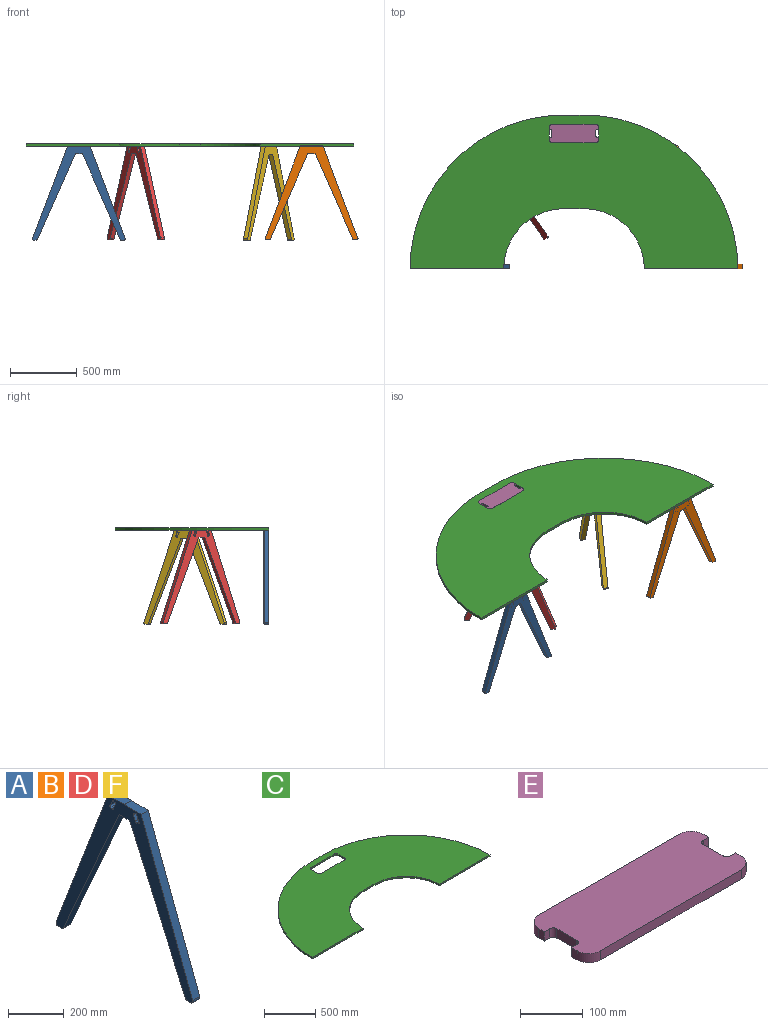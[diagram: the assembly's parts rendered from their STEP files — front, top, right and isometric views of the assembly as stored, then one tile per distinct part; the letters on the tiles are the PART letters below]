
ASSEMBLY  parts=6 mates=1
PART A: 38 faces, bbox 36x694.1x702 mm
  f0: plane 702.04x694.13mm, normal (-1,0,0), area 86384.5mm2, adj f1,f2,f3,f4,f5,f6,f7,f8
  f1: plane 36x27mm, normal (0,0,-1), area 971.9mm2, adj f0,f2,f18,f19
  f2: plane 36x0mm, normal (0,-0.85,0.53), area 0.2mm2, adj f0,f1,f3,f19
  f3: plane 638.9x282.02mm, normal (0,-0.91,-0.4), area 25141.4mm2, adj f0,f2,f4,f19
  f4: cylinder r=10mm len=36mm, axis (-1,0,0), area 415.8mm2, adj f0,f3,f5,f19
  f5: plane 36x18.89mm, normal (0,0,-1), area 680.2mm2, adj f0,f4,f6,f19
  f6: cylinder r=10mm len=36mm, axis (-1,0,0), area 696.3mm2, adj f0,f5,f7,f19
  f7: plane 688.47x261.77mm, normal (0,0.93,0.36), area 26516.1mm2, adj f0,f6,f8,f19
  f8: plane 82.88x36mm, normal (0,0,1), area 2983.7mm2, adj f0,f7,f9,f19
  f9: plane 36x0mm, normal (0,0.6,-0.8), area 0mm2, adj f0,f8,f10,f19
  f10: plane 36x1.76mm, normal (0,0,1), area 63.3mm2, adj f0,f9,f11,f19
  f11: plane 84.64x36mm, normal (0,0,1), area 3046.9mm2, adj f0,f10,f12,f19
  f12: plane 688.47x261.78mm, normal (0,-0.93,0.36), area 26516.1mm2, adj f0,f11,f13,f19
  f13: cylinder r=10mm len=36mm, axis (-1,0,0), area 696.3mm2, adj f0,f12,f14,f19
  f14: plane 36x18.89mm, normal (0,0,-1), area 680.2mm2, adj f0,f13,f15,f19
  f15: cylinder r=10mm len=36mm, axis (-1,0,0), area 415.8mm2, adj f0,f14,f16,f19
  f16: plane 636.51x280.97mm, normal (0,0.91,-0.4), area 25047.5mm2, adj f0,f15,f17,f19
  f17: cylinder r=4mm len=36mm, axis (-1,0,0), area 166.3mm2, adj f0,f16,f18,f19
  f18: plane 36x24.39mm, normal (0,0,-1), area 878mm2, adj f0,f1,f17,f19
  f19: plane 702.04x694.13mm, normal (1,0,0), area 87734.9mm2, adj f1,f2,f3,f4,f5,f6,f7,f8
  f20: cylinder r=4mm len=30mm, axis (-1,0,0), area 378.8mm2, adj f0,f21,f27,f28
  f21: plane 30x6.16mm, normal (0,0.39,-0.92), area 200.5mm2, adj f0,f20,f22,f28
  f22: cylinder r=4mm len=30mm, axis (-1,0,0), area 378.6mm2, adj f0,f21,f23,f28
  f23: plane 30x22.61mm, normal (0,0.92,0.39), area 738.2mm2, adj f0,f22,f24,f28
  f24: cylinder r=4mm len=30mm, axis (-1,0,0), area 378.6mm2, adj f0,f23,f25,f28
  f25: plane 30x5.8mm, normal (0,-0.39,0.92), area 188.5mm2, adj f0,f24,f26,f28
  f26: cylinder r=4mm len=30mm, axis (-1,0,0), area 378.8mm2, adj f0,f25,f27,f28
  f27: plane 30x22.77mm, normal (0,-0.93,-0.38), area 738.1mm2, adj f0,f20,f26,f28
  f28: plane 40.67x30.93mm, normal (-1,0,0), area 675.2mm2, adj f20,f21,f22,f23,f24,f25,f26,f27
  f29: plane 30x6.16mm, normal (0,-0.39,-0.92), area 200.5mm2, adj f0,f30,f36,f37
  f30: cylinder r=4mm len=30mm, axis (-1,0,0), area 378.8mm2, adj f0,f29,f31,f37
  f31: plane 30x22.77mm, normal (0,0.93,-0.38), area 738.1mm2, adj f0,f30,f32,f37
  f32: cylinder r=4mm len=30mm, axis (-1,0,0), area 378.8mm2, adj f0,f31,f33,f37
  f33: plane 30x5.8mm, normal (0,0.39,0.92), area 188.5mm2, adj f0,f32,f34,f37
  f34: cylinder r=4mm len=30mm, axis (-1,0,0), area 378.6mm2, adj f0,f33,f35,f37
  f35: plane 30x22.61mm, normal (0,-0.92,0.39), area 738.2mm2, adj f0,f34,f36,f37
  f36: cylinder r=4mm len=30mm, axis (-1,0,0), area 378.6mm2, adj f0,f29,f35,f37
  f37: plane 40.67x30.93mm, normal (-1,0,0), area 675.2mm2, adj f29,f30,f31,f32,f33,f34,f35,f36
PART B: same geometry as A
PART C: 18 faces, bbox 2450x1150x18 mm
  f0: cylinder r=26.8mm len=26.8mm, axis (0,0,-1), area 757.8mm2, adj f1,f15,f16,f17
  f1: plane 316x18mm, normal (0,1,0), area 5688mm2, adj f0,f2,f16,f17
  f2: cylinder r=26.8mm len=26.8mm, axis (0,0,-1), area 757.8mm2, adj f1,f3,f16,f17
  f3: plane 86x18mm, normal (1,0,0), area 1548mm2, adj f2,f4,f16,f17
  f4: cylinder r=26.8mm len=26.8mm, axis (0,0,-1), area 757.8mm2, adj f3,f5,f16,f17
  f5: plane 316x18mm, normal (0,-1,0), area 5688mm2, adj f4,f6,f16,f17
  f6: cylinder r=26.8mm len=26.8mm, axis (0,0,-1), area 757.8mm2, adj f5,f15,f16,f17
  f7: cylinder r=450mm len=450mm, axis (0,0,-1), area 12723.5mm2, adj f8,f14,f16,f17
  f8: plane 150x18mm, normal (0,-1,0), area 2700mm2, adj f7,f9,f16,f17
  f9: cylinder r=450mm len=450mm, axis (0,0,-1), area 12723.5mm2, adj f8,f10,f16,f17
  f10: plane 700x18mm, normal (0,-1,0), area 12600mm2, adj f9,f11,f16,f17
  f11: cylinder r=1150mm len=1150mm, axis (0,0,-1), area 32515.5mm2, adj f10,f12,f16,f17
  f12: plane 150x18mm, normal (0,1,0), area 2700mm2, adj f11,f13,f16,f17
  f13: cylinder r=1150mm len=1150mm, axis (0,0,-1), area 32515.5mm2, adj f12,f14,f16,f17
  f14: plane 700x18mm, normal (0,-1,0), area 12600mm2, adj f7,f13,f16,f17
  f15: plane 86x18mm, normal (-1,0,0), area 1548mm2, adj f0,f6,f16,f17
  f16: plane 2450x1150mm, normal (0,0,1), area 1813312.3mm2, adj f0,f1,f2,f3,f4,f5,f6,f7
  f17: plane 2450x1150mm, normal (0,0,-1), area 1813312.3mm2, adj f0,f1,f2,f3,f4,f5,f6,f7
PART D: same geometry as A
PART E: 22 faces, bbox 369x139.1x18 mm
  f0: cylinder r=8mm len=18mm, axis (0,0,-1), area 226.2mm2, adj f1,f19,f20,f21
  f1: plane 45x18mm, normal (1,0,0), area 810mm2, adj f0,f2,f20,f21
  f2: cylinder r=8mm len=18mm, axis (0,0,-1), area 226.2mm2, adj f1,f3,f20,f21
  f3: plane 18x12.11mm, normal (0,-1,0), area 218mm2, adj f2,f4,f20,f21
  f4: plane 18x12.5mm, normal (1,0,0), area 225mm2, adj f3,f5,f20,f21
  f5: cylinder r=26.5mm len=26.51mm, axis (0,0,-1), area 749.3mm2, adj f4,f6,f20,f21
  f6: plane 316x18mm, normal (0,1,0), area 5688mm2, adj f5,f7,f20,f21
  f7: cylinder r=26.5mm len=26.51mm, axis (0,0,-1), area 749.3mm2, adj f6,f8,f20,f21
  f8: plane 18x12.5mm, normal (-1,0,0), area 225mm2, adj f7,f9,f20,f21
  f9: plane 18x12.11mm, normal (0,-1,0), area 218mm2, adj f8,f10,f20,f21
  f10: cylinder r=8mm len=18mm, axis (0,0,-1), area 226.2mm2, adj f9,f11,f20,f21
  f11: plane 45x18mm, normal (-1,0,0), area 810mm2, adj f10,f12,f20,f21
  f12: cylinder r=8mm len=18mm, axis (0,0,-1), area 226.2mm2, adj f11,f13,f20,f21
  f13: plane 18x12.11mm, normal (0,1,0), area 218mm2, adj f12,f14,f20,f21
  f14: plane 18x12.5mm, normal (-1,0,0), area 225mm2, adj f13,f15,f20,f21
  f15: cylinder r=26.5mm len=26.51mm, axis (0,0,-1), area 749.3mm2, adj f14,f16,f20,f21
  f16: plane 316x18mm, normal (0,-1,0), area 5688mm2, adj f15,f17,f20,f21
  f17: cylinder r=26.5mm len=26.51mm, axis (0,0,-1), area 749.3mm2, adj f16,f18,f20,f21
  f18: plane 18x12.5mm, normal (1,0,0), area 225mm2, adj f17,f19,f20,f21
  f19: plane 18x12.11mm, normal (0,1,0), area 218mm2, adj f0,f18,f20,f21
  f20: plane 369.03x139.11mm, normal (0,0,1), area 48289.8mm2, adj f0,f1,f2,f3,f4,f5,f6,f7
  f21: plane 369.03x139.11mm, normal (0,0,-1), area 48289.8mm2, adj f0,f1,f2,f3,f4,f5,f6,f7
PART F: same geometry as A
PLACE A rot(axis=(0,0,-1),90deg) t=(-628.15,-332.37,-227.55)mm
PLACE B rot(axis=(0,0,-1),90deg) t=(1110.28,-331.27,-225.69)mm
PLACE C t=(202.12,205.72,124.54)mm
PLACE D rot(axis=(0,0,1),35deg) t=(-217.52,133.47,-224.54)mm
PLACE E rot(axis=(0,0,1),0deg) t=(201.8,643.65,124.54)mm
PLACE F rot(axis=(0,0,-1),30deg) t=(775.74,264.97,-228.62)mm
MATE planar E.f6 <-> C.f5  axis (0,1,0) through (201.8,713.15,133.54)mm
